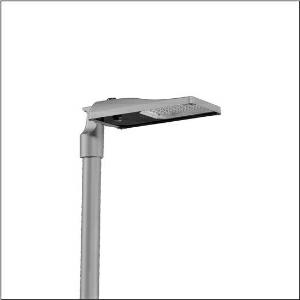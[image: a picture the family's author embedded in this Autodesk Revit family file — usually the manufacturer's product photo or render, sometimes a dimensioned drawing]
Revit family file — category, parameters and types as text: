
# Revit family: streetlight_sl_31_mini___stw1_0a_5xh6e31t08ga_7388
name_source: partatom
category: Lighting Fixtures
units: mm (PartAtom-declared; Revit-internal decimal feet)

## family parameters
Cut with Voids When Loaded = No
Host = Face
Light Source = No
Part Type = Normal
Room Calculation Point = No
Round Connector Dimension = Use Diameter
Shared = No

## types (1)
- --- (1 x LED, 5880 lm, 39.3 W, 3000K)
    Apparent Load = 39 VA
    CIE Flux Codes = 38 75 98 100 100
    Color Rendering = 70
    Color Temperature = 3000K
    Default Elevation = 1800 mm
    Description = Streetlight SL 31 mini D4i, Desk-Remote mast luminaire for post-top, side-entry; light control with lens of PMMA; light distribution: STW1.0a, direct asymmetric distribution, for standard-compliant lighting for roads and squares; LED: luminous flux: 5.880lm, light colour: 730, colour temperature: 3000K; luminous efficacy: 149,6lm/W; control: pre-setting: logarithmic dimming characteristic, flexible luminous flux parameterisation, time-dependent luminous flux control, constant luminous flux control, power reduction, intelligent temperature release in ECG and LED module, overheat protection; luminaire housing, of diecast aluminium, Siteco® metallic grey (DB 702S), corrosivity category C5 high according to DIN EN ISO 12944; cover of toughened safety glass, transparent, opened without tools; mast flange of diecast aluminium, Siteco® metallic grey (DB 702S), spigot size: 76/60mm, mast flange included unmounted; with cable H07RN-F 2x 1.5mm², cable length: 6,5m, connection cable pre-assembled; mains connection: 220..240V, AC, 50/60Hz; power consumption (at start of service life): 39,3W / (at end of service life): 40,7W / (with reduced operation 50%): 18,1W; protection rating (complete): IP66; insulation class (complete): insulation class II (safety insulation); impact resistance: IK09; certification: CE, ENEC, ENEC+, VDE, UKCA, ZD4i; permissible operating ambient temperature for outdoor applications: -40..+50°C; packaging unit: 1 piece

Light Distribution: STW1.0a
    Height = 76 mm
    Lamp = 1 x LED
    Lamp Light Flux = 5880 lm
    Lamp Power = 39.3 W
    Lamp count = 1
    Length = 547 mm
    Luminous efficacy = 150 lm/W
    Manufacturer = Siteco
    ModVariant = No
    Model = 5XH6E31T08GA
    Number of Poles = 1
    OnlyDefault = Yes
    Power Factor = 1
    Product Name = Streetlight SL 31 mini | STW1.0a
    Product group = mast luminaire | pylon top
    ProductGroupID = 6100
    Protection Class = Protection class II
    Protection Degree = IP 66
    RLX_Detail_Level = 1
    RLX_Emergency_Light_Flux = 0 lm
    RLX_Emergency_Type = 0
    RLX_Emergency_Type_DB = No
    RlxData = <blob elided: 39825 chars, md5=e0394000>
    Socket = socket
    Standby Power = 0 W
    System Light Flux = 5880 lm
    System Power = 39 W
    Type Comments = factory setting: luminous flux: 100 % | dim-lin: 254 | 798 mA
    Type Image = l_1300332.jpg
    URL = http://relux.com
    VarID = @adj_053526
    Voltage = 0 V
    Weight = 0.00 kg
    Width = 265 mm

## geometry (parser evidence)
native form markers: Blend x4, Sweep x11
no freeform markers — native parametric forms only
